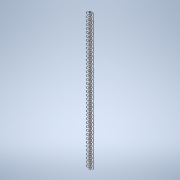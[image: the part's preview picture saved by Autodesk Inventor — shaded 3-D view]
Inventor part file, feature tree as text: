
AUTODESK INVENTOR PART (.ipt)
format: ipt  version: 2020 (Build 240168000, 168)  size: 510,976 bytes
history: native  units: mm
features: sketch x3, extrude x2, helix x1, pattern_linear x1
ambient origin geometry x8: Origin, YZ Plane, XZ Plane, XY Plane, X Axis, Y Axis, Z Axis, Center Point
bodies: Solid1 (feature_tree)
feature tree (7):
  extrude  "Extrusion1"  Depth=800.0mm TaperAngle=0.0deg
  helix  "Coil1"  [1 undecoded]
  extrude  "Extrusion2"  Depth=2.0mm
  pattern_linear  "Rectangular Pattern1"  Spacing1=2.0mm  [1 undecoded]
  sketch  "Sketch1"  dims[d0=10.0mm d1=800.0mm d2=0.0mm d3=2.0mm]
  sketch  "Sketch2"  dims[d4=10.0mm d5=2.0mm]
  sketch  "Sketch3"  dims[d6=20.0mm d7=10.0mm d8=400.0mm d9=0.0mm d10=90.0deg d11=90.0deg d12=0.0mm d13=0.0mm d14=2.0mm d15=30.0deg d16=160.0mm d18=20.0mm]
note: 2 required parameter values undecoded (feature->parameter linkage not recoverable at this tier; creation-order binding heuristic only, values carry confidence <= 0.55)
